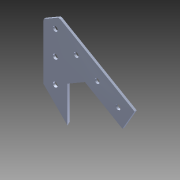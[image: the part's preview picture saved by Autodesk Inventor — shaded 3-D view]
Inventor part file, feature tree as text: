
AUTODESK INVENTOR PART (.ipt)
format: ipt  version: 2015 SP1 (Build 190203100, 203)  size: 230,400 bytes
history: native  units: in
note: dims shown in document units (in); Inventor stores cm internally (conversion verified against a paired STEP export)
features: extrude x5, sketch x5, projected_geometry x4, other x2, imported_body x1
ambient origin geometry x8: Origin, YZ Plane, XZ Plane, XY Plane, X Axis, Y Axis, Z Axis, Center Point
bodies: Body1 (feature_tree)
feature tree (17):
  other  "Cut-Extrude2"
  other  "Versaframe 60deg gusset1"
  extrude  "Extrusion3"  Depth=1.5in TaperAngle=0.0deg
  extrude  "Extrusion4"  Depth=0.09in
  extrude  "Extrusion5"  Depth=0.2in
  extrude  "Extrusion6"  Depth=0.2in
  extrude  "Extrusion7"  Depth=0.09in
  imported_body  "Base1"
  sketch  "Sketch3"  dims[d14=1.5in d15=0.0in d16=1.5in d17=0.0in]
  projected_geometry  "Projected Loop2"
  projected_geometry  "Projected Loop3"
  sketch  "Sketch4"  dims[d18=0.09in d19=0.0in d20=0.2in]
  projected_geometry  "Projected Loop4"
  projected_geometry  "Projected Loop5"
  sketch  "Sketch5"  dims[d21=0.2in d22=0.2in]
  sketch  "Sketch6"  dims[d23=0.2in d24=0.2in]
  sketch  "Sketch7"  dims[d25=0.2in d26=0.2in d27=0.5in d28=1.0in d29=0.5in d30=0.5in d31=0.09in d32=0.0in d33=0.09in d34=0.0in]
